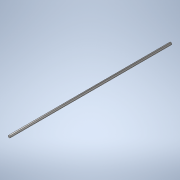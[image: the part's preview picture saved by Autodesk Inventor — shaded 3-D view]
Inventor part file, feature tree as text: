
AUTODESK INVENTOR PART (.ipt)
format: ipt  version: 2020 (Build 240168000, 168)  size: 111,616 bytes
history: native  units: in
note: dims shown in document units (in); Inventor stores cm internally (conversion verified against a paired STEP export)
features: extrude x1, sketch x1
ambient origin geometry x8: Origin, YZ Plane, XZ Plane, XY Plane, X Axis, Y Axis, Z Axis, Center Point
bodies: Solid1 (feature_tree)
feature tree (2):
  extrude  "Extrusion1"  Depth=40.0in TaperAngle=0.0deg
  sketch  "Sketch1"  dims[d0=0.5in d1=40.0in d2=0.0in]
